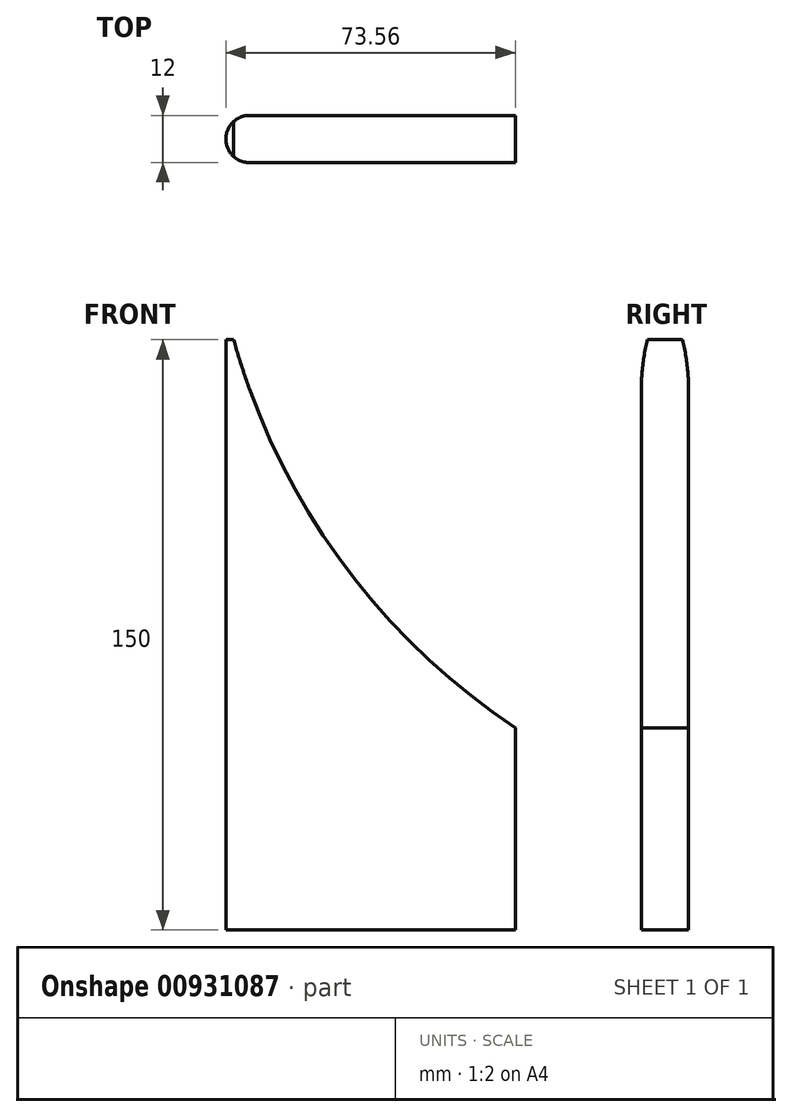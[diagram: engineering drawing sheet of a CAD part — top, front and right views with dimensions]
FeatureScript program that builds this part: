
annotation { "Feature Type Name" : "Feature", "Feature Type Description" : "" }
export const myFeature = defineFeature(function(context is Context, id is Id, definition is map)
    precondition{}
    {
        {
            var Q0;
            Q0=qCreatedBy(makeId("Front.planeOp"),FACE);
            var sketch = newSketch(context, id + "F0", { "sketchPlane" : qUnion([Q0])});
            skLineSegment(sketch, "E0.bottom", {"start": v(-44.44, -20.66) * mm, "end": v(-118, -20.66) * mm});
            skArc(sketch, "E1", {"start": v(-116, 129.34) * mm, "mid": v(-89.08, 73.6) * mm, "end": v(-44.44, 30.72) * mm});
            skPoint(sketch, "E2.orphan", {"position": v(-4.44, 176.38) * mm});
            skLineSegment(sketch, "E3", {"start": v(-44.44, -20.66) * mm, "end": v(-44.44, 30.72) * mm});
            skLineSegment(sketch, "E4", {"start": v(-118, 129.34) * mm, "end": v(-118, -20.66) * mm});
            skLineSegment(sketch, "E5", {"start": v(-116, 129.34) * mm, "end": v(-118, 129.34) * mm});
            skSolve(sketch);
        }
        {
            var Q0;
            Q0=makeQuery(id+"F0.imprint","IMPRINT",FACE,{"disambiguationData":[TD([[makeQuery(id+"F0.imprint","IMPRINT",EDGE,{"derivedFrom":sQuery(id+"F0.wireOp",EDGE,"E0.bottom")}),-1.0]])]});
            extrude(context, id + "F1", {"entities" : qUnion([Q0]), "depth" : 12 * mm, "offsetDistance" : 25 * mm});
        }
        {
            var Q0;
            Q0=makeQuery(id+"F1.opExtrude","CAP_EDGE",EDGE,{"disambiguationData":[OSD([sQuery(id+"F0.wireOp",EDGE,"E4")])],"isStart":true});
            var Q1;
            Q1=makeQuery(id+"F1.opExtrude","CAP_EDGE",EDGE,{"disambiguationData":[OSD([sQuery(id+"F0.wireOp",EDGE,"E4")])],"isStart":false});
            fillet(context, id + "F2", {"entities" : qUnion([Q0, Q1]), "tangentPropagation" : true, "radius" : 6 * mm, "defaultsChanged" : true, "vertexSettings" : [], "allowEdgeOverflow" : false});
        }
    });
